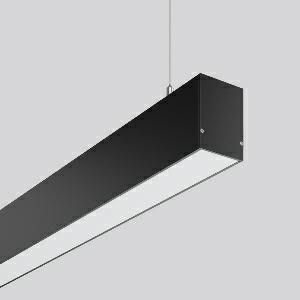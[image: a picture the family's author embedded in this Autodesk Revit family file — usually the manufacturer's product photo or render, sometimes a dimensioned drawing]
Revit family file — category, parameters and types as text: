
# Revit family: less_is_more_50_312321_003_19e1
name_source: partatom
category: Lighting Fixtures
units: mm (PartAtom-declared; Revit-internal decimal feet)

## family parameters
Cut with Voids When Loaded = No
Host = Face
Light Source = No
Part Type = Normal
Room Calculation Point = No
Round Connector Dimension = Use Diameter
Shared = No

## types (1)
- LESS IS MORE 50 (1 x LED Modul 830, 8450 lm, 3000)
    Apparent Load = 74 VA
    CIE Flux Codes = 49 80 96 63 100
    Color Rendering = 80
    Color Temperature = 3000
    Default Elevation = 1800 mm
    Description = Series: LESS IS MORE 50
Linear pendant luminaire for aesthetically sophisticated lighting. Housing: extruded aluminium profile, powder-coated. End cap aluminium powder-coated. Canopy made of aluminium, powder-coated. Diffuser made of non-yellowing plastic (PMMA), opal. Direct 65%, indirect 35% light emission. Suitable for pendant. 2-point steel cable suspension freely positionable and infinitely height-adjustable. Special lengths available on request. LED unit with integrated converter interchangeable and removable. Suitable for through-wiring. With sensors or as a safety luminaire on request. 
Colour: deep black, matt (RAL 9005)
Length: 1967 mm
Width: 57 mm
Height: 75 mm
Suspension length: 2000 mm
Lamp: LED
Socket: without socket
Colour temperature: 3000K
Colour rendering index (CRI): 80
Light source: LED
Socket lamp2: Without base
Colour temperature: 3000K
System power: 74 W
Rated luminous flux: 8450 lm
Luminous efficiency: 114 lm/W
Control gear: Regulated power supply
Control gear: Regulated power supply
Protection class: I
Type of protection: IP 20
    Height = 75 mm
    Lamp = 1 x LED Modul 830
    Lamp Light Flux = 8450 lm
    Lamp count = 1
    Length = 1967 mm
    Lifetime = 50000 h
    Luminous efficacy = 114 lm/W
    Manufacturer = RZB
    ModVariant = No
    Model = 312321.003
    Mounting Place = Ceiling
    Mounting Type = Pendant
    Number of Poles = 1
    OnlyDefault = Yes
    Power Factor = 1
    Product Name = LESS IS MORE 50
    Product group = Pendant LED linear luminaires
    ProductGroupID = 907
    Protection Class = Protection class I
    Protection Degree = IP 20
    RLX_Detail_Level = 1
    RLX_Emergency_Light_Flux = 0 lm
    RLX_Emergency_Type = 0
    RLX_Emergency_Type_DB = No
    RlxData = <blob elided: 39881 chars, md5=4a3fe425>
    Socket = socket
    Standby Power = 0 W
    System Light Flux = 8450 lm
    System Power = 74 W
    Type Comments = Product without accessories
    Type Image = 312318.003.jpg
    URL = http://relux.com
    VarID = ---
    Voltage = 230 V
    Voltage Range = 220-240 V
    Weight = 0.00 kg
    Width = 57 mm

## geometry (parser evidence)
native form markers: Blend x4, Sweep x13
no freeform markers — native parametric forms only
